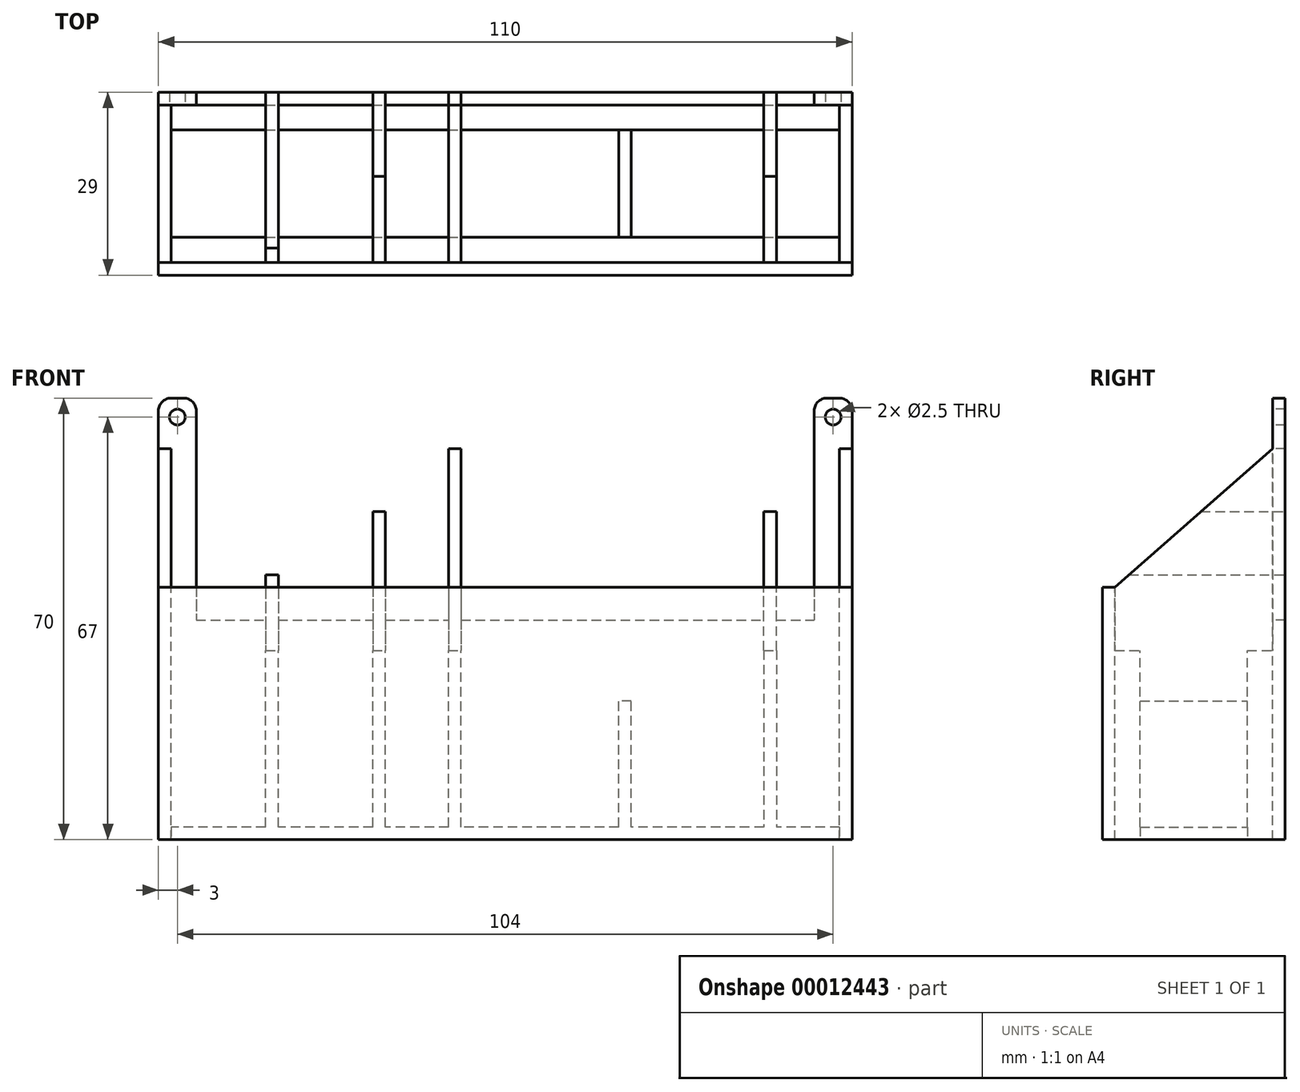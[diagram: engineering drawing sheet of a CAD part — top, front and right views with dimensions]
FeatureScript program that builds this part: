
annotation { "Feature Type Name" : "Feature", "Feature Type Description" : "" }
export const myFeature = defineFeature(function(context is Context, id is Id, definition is map)
    precondition{}
    {
        {
            var Q0;
            Q0=qCreatedBy(makeId("Front.planeOp"),FACE);
            var sketch = newSketch(context, id + "F0", { "sketchPlane" : qUnion([Q0])});
            skLineSegment(sketch, "E0.bottom", {"start": v(0, 0) * mm, "end": v(-110, 0) * mm});
            skLineSegment(sketch, "E0.top", {"start": v(-2, 70) * mm, "end": v(-108, 70) * mm});
            skLineSegment(sketch, "E0.left", {"start": v(0, 0) * mm, "end": v(0, 68) * mm});
            skLineSegment(sketch, "E0.right", {"start": v(-110, 0) * mm, "end": v(-110, 68) * mm});
            skPoint(sketch, "E1.visualSharp", {"position": v(0, 70) * mm});
            skArc(sketch, "E1.filletArc", {"start": v(0, 68) * mm, "mid": v(-0.59, 69.41) * mm, "end": v(-2, 70) * mm});
            skPoint(sketch, "E2.visualSharp", {"position": v(-110, 70) * mm});
            skArc(sketch, "E2.filletArc", {"start": v(-108, 70) * mm, "mid": v(-109.41, 69.41) * mm, "end": v(-110, 68) * mm});
            skSolve(sketch);
        }
        {
            var Q0;
            Q0 = qSketchRegion(id + "F0", true);
            extrude(context, id + "F1", {"entities" : qUnion([Q0]), "oppositeDirection" : true, "depth" : 2 * mm});
        }
        {
            var Q0;
            Q0=makeQuery(id+"F1.opExtrude","CAP_FACE",FACE,{"disambiguationData":[OSD([sQuery(id+"F0.wireOp",EDGE,"E0.bottom"),sQuery(id+"F0.wireOp",EDGE,"E0.top"),sQuery(id+"F0.wireOp",EDGE,"E0.left"),sQuery(id+"F0.wireOp",EDGE,"E0.right")])],"isStart":true});
            var sketch = newSketch(context, id + "F2", { "sketchPlane" : qUnion([Q0])});
            skLineSegment(sketch, "E3.bottom", {"start": v(-110, 2) * mm, "end": v(0, 2) * mm});
            skLineSegment(sketch, "E3.top", {"start": v(-110, 0) * mm, "end": v(0, 0) * mm});
            skLineSegment(sketch, "E3.left", {"start": v(-110, 2) * mm, "end": v(-110, 0) * mm});
            skLineSegment(sketch, "E3.right", {"start": v(0, 2) * mm, "end": v(0, 0) * mm});
            skLineSegment(sketch, "E4.bottom", {"start": v(0, 2) * mm, "end": v(-2, 2) * mm});
            skLineSegment(sketch, "E4.top", {"start": v(0, 62) * mm, "end": v(-2, 62) * mm});
            skLineSegment(sketch, "E4.left", {"start": v(0, 2) * mm, "end": v(0, 62) * mm});
            skLineSegment(sketch, "E4.right", {"start": v(-2, 2) * mm, "end": v(-2, 62) * mm});
            skLineSegment(sketch, "E5.bottom", {"start": v(-110, 2) * mm, "end": v(-108, 2) * mm});
            skLineSegment(sketch, "E5.top", {"start": v(-110, 62) * mm, "end": v(-108, 62) * mm});
            skLineSegment(sketch, "E5.left", {"start": v(-110, 2) * mm, "end": v(-110, 62) * mm});
            skLineSegment(sketch, "E5.right", {"start": v(-108, 2) * mm, "end": v(-108, 62) * mm});
            skLineSegment(sketch, "E6.bottom", {"start": v(-93, 42) * mm, "end": v(-91, 42) * mm});
            skLineSegment(sketch, "E6.top", {"start": v(-93, 2) * mm, "end": v(-91, 2) * mm});
            skLineSegment(sketch, "E6.left", {"start": v(-93, 42) * mm, "end": v(-93, 2) * mm});
            skLineSegment(sketch, "E6.right", {"start": v(-91, 42) * mm, "end": v(-91, 2) * mm});
            skLineSegment(sketch, "E7.bottom", {"start": v(-76, 52) * mm, "end": v(-74, 52) * mm});
            skLineSegment(sketch, "E7.top", {"start": v(-76, 2) * mm, "end": v(-74, 2) * mm});
            skLineSegment(sketch, "E7.left", {"start": v(-76, 52) * mm, "end": v(-76, 2) * mm});
            skLineSegment(sketch, "E7.right", {"start": v(-74, 52) * mm, "end": v(-74, 2) * mm});
            skLineSegment(sketch, "E8.bottom", {"start": v(-64, 62) * mm, "end": v(-62, 62) * mm});
            skLineSegment(sketch, "E8.top", {"start": v(-64, 2) * mm, "end": v(-62, 2) * mm});
            skLineSegment(sketch, "E8.left", {"start": v(-64, 62) * mm, "end": v(-64, 2) * mm});
            skLineSegment(sketch, "E8.right", {"start": v(-62, 62) * mm, "end": v(-62, 2) * mm});
            skLineSegment(sketch, "E9.bottom", {"start": v(-37, 22) * mm, "end": v(-35, 22) * mm});
            skLineSegment(sketch, "E9.top", {"start": v(-37, 2) * mm, "end": v(-35, 2) * mm});
            skLineSegment(sketch, "E9.left", {"start": v(-37, 22) * mm, "end": v(-37, 2) * mm});
            skLineSegment(sketch, "E9.right", {"start": v(-35, 22) * mm, "end": v(-35, 2) * mm});
            skLineSegment(sketch, "E10.bottom", {"start": v(-12, 2) * mm, "end": v(-14, 2) * mm});
            skLineSegment(sketch, "E10.top", {"start": v(-12, 52) * mm, "end": v(-14, 52) * mm});
            skLineSegment(sketch, "E10.left", {"start": v(-12, 2) * mm, "end": v(-12, 52) * mm});
            skLineSegment(sketch, "E10.right", {"start": v(-14, 2) * mm, "end": v(-14, 52) * mm});
            skSolve(sketch);
        }
        {
            var Q0;
            Q0 = qSketchRegion(id + "F2", true);
            extrude(context, id + "F3", {"entities" : qUnion([Q0]), "operationType" : NewBodyOperationType.ADD, "depth" : 25 * mm});
        }
        {
            var Q0;
            Q0=makeQuery(id+"F3.opExtrude","CAP_FACE",FACE,{"disambiguationData":[OSD([sQuery(id+"F2.wireOp",EDGE,"E3.bottom"),sQuery(id+"F2.wireOp",EDGE,"E3.top"),sQuery(id+"F2.wireOp",EDGE,"E3.left"),sQuery(id+"F2.wireOp",EDGE,"E3.right"),sQuery(id+"F2.wireOp",EDGE,"E4.top"),sQuery(id+"F2.wireOp",EDGE,"E4.left"),sQuery(id+"F2.wireOp",EDGE,"E4.right"),sQuery(id+"F2.wireOp",EDGE,"E5.top"),sQuery(id+"F2.wireOp",EDGE,"E5.left"),sQuery(id+"F2.wireOp",EDGE,"E5.right"),sQuery(id+"F2.wireOp",EDGE,"E6.bottom"),sQuery(id+"F2.wireOp",EDGE,"E6.left"),sQuery(id+"F2.wireOp",EDGE,"E6.right"),sQuery(id+"F2.wireOp",EDGE,"E7.bottom"),sQuery(id+"F2.wireOp",EDGE,"E7.left"),sQuery(id+"F2.wireOp",EDGE,"E7.right"),sQuery(id+"F2.wireOp",EDGE,"E8.bottom"),sQuery(id+"F2.wireOp",EDGE,"E8.left"),sQuery(id+"F2.wireOp",EDGE,"E8.right"),sQuery(id+"F2.wireOp",EDGE,"E9.bottom"),sQuery(id+"F2.wireOp",EDGE,"E9.left"),sQuery(id+"F2.wireOp",EDGE,"E9.right")])],"isStart":false});
            var sketch = newSketch(context, id + "F4", { "sketchPlane" : qUnion([Q0])});
            skLineSegment(sketch, "E11.bottom", {"start": v(-110, 0) * mm, "end": v(0, 0) * mm});
            skLineSegment(sketch, "E11.top", {"start": v(-110, 40) * mm, "end": v(0, 40) * mm});
            skLineSegment(sketch, "E11.left", {"start": v(-110, 0) * mm, "end": v(-110, 40) * mm});
            skLineSegment(sketch, "E11.right", {"start": v(0, 0) * mm, "end": v(0, 40) * mm});
            skSolve(sketch);
        }
        {
            var Q0;
            Q0 = qSketchRegion(id + "F4", true);
            extrude(context, id + "F5", {"entities" : qUnion([Q0]), "operationType" : NewBodyOperationType.ADD, "depth" : 2 * mm});
        }
        {
            var Q0;
            Q0=makeQuery(id+"F1.opExtrude","CAP_FACE",FACE,{"disambiguationData":[OSD([sQuery(id+"F0.wireOp",EDGE,"E0.bottom"),sQuery(id+"F0.wireOp",EDGE,"E0.top"),sQuery(id+"F0.wireOp",EDGE,"E0.left"),sQuery(id+"F0.wireOp",EDGE,"E0.right")])],"isStart":true});
            var sketch = newSketch(context, id + "F6", { "sketchPlane" : qUnion([Q0])});
            skCircle(sketch, "E12", {"center": v(-107, 67) * mm, "radius": 1.25 * mm});
            skCircle(sketch, "E13", {"center": v(-3, 67) * mm, "radius": 1.25 * mm});
            skSolve(sketch);
        }
        {
            var Q0;
            Q0 = qSketchRegion(id + "F6", true);
            extrude(context, id + "F7", {"entities" : qUnion([Q0]), "operationType" : NewBodyOperationType.REMOVE, "oppositeDirection" : true, "depth" : 2 * mm});
        }
        {
            var Q0;
            Q0=makeQuery(id+"F5.boolean.opBoolean","MERGE",FACE,{"derivedFrom":[makeQuery(id+"F3.boolean.opBoolean","MERGE",FACE,{"derivedFrom":[makeQuery(id+"F1.opExtrude","SWEPT_FACE",FACE,{"disambiguationData":[OSD([sQuery(id+"F0.wireOp",EDGE,"E0.right")])]}),makeQuery(id+"F3.opExtrude","SWEPT_FACE",FACE,{"disambiguationData":[OSD([sQuery(id+"F2.wireOp",EDGE,"E3.left"),sQuery(id+"F2.wireOp",EDGE,"E5.left")])]})]}),makeQuery(id+"F5.opExtrude","SWEPT_FACE",FACE,{"disambiguationData":[OSD([sQuery(id+"F4.wireOp",EDGE,"E11.left")])]})]});
            var sketch = newSketch(context, id + "F8", { "sketchPlane" : qUnion([Q0])});
            skLineSegment(sketch, "E14", {"start": v(25, 62) * mm, "end": v(25, 40) * mm});
            skLineSegment(sketch, "E15", {"start": v(25, 40) * mm, "end": v(0, 62) * mm});
            skLineSegment(sketch, "E16", {"start": v(0, 62) * mm, "end": v(25, 62) * mm});
            skSolve(sketch);
        }
        {
            var Q0;
            Q0 = qSketchRegion(id + "F8", true);
            extrude(context, id + "F9", {"entities" : qUnion([Q0]), "operationType" : NewBodyOperationType.REMOVE, "oppositeDirection" : true, "depth" : 110 * mm});
        }
        {
            var Q0;
            Q0=makeQuery(id+"F5.boolean.opBoolean","MERGE",FACE,{"derivedFrom":[makeQuery(id+"F3.boolean.opBoolean","MERGE",FACE,{"derivedFrom":[makeQuery(id+"F1.opExtrude","SWEPT_FACE",FACE,{"disambiguationData":[OSD([sQuery(id+"F0.wireOp",EDGE,"E0.bottom")])]}),makeQuery(id+"F3.opExtrude","SWEPT_FACE",FACE,{"disambiguationData":[OSD([sQuery(id+"F2.wireOp",EDGE,"E3.top")])]})]}),makeQuery(id+"F5.opExtrude","SWEPT_FACE",FACE,{"disambiguationData":[OSD([sQuery(id+"F4.wireOp",EDGE,"E11.bottom")])]})]});
            var sketch = newSketch(context, id + "F10", { "sketchPlane" : qUnion([Q0])});
            skLineSegment(sketch, "E17.bottom", {"start": v(-108, 0) * mm, "end": v(-2, 0) * mm});
            skLineSegment(sketch, "E17.top", {"start": v(-108, 4) * mm, "end": v(-2, 4) * mm});
            skLineSegment(sketch, "E17.left", {"start": v(-108, 0) * mm, "end": v(-108, 4) * mm});
            skLineSegment(sketch, "E17.right", {"start": v(-2, 0) * mm, "end": v(-2, 4) * mm});
            skLineSegment(sketch, "E18.bottom", {"start": v(-108, 21) * mm, "end": v(-2, 21) * mm});
            skLineSegment(sketch, "E18.top", {"start": v(-108, 25) * mm, "end": v(-2, 25) * mm});
            skLineSegment(sketch, "E18.left", {"start": v(-108, 21) * mm, "end": v(-108, 25) * mm});
            skLineSegment(sketch, "E18.right", {"start": v(-2, 21) * mm, "end": v(-2, 25) * mm});
            skSolve(sketch);
        }
        {
            var Q0;
            Q0 = qSketchRegion(id + "F10", true);
            extrude(context, id + "F11", {"entities" : qUnion([Q0]), "operationType" : NewBodyOperationType.REMOVE, "oppositeDirection" : true, "depth" : 30 * mm});
        }
        {
            var Q0;
            Q0=makeQuery(id+"F11.boolean.opBoolean","MERGE",FACE,{"derivedFrom":[makeQuery(id+"F1.opExtrude","CAP_FACE",FACE,{"disambiguationData":[OSD([sQuery(id+"F0.wireOp",EDGE,"E0.bottom"),sQuery(id+"F0.wireOp",EDGE,"E0.top"),sQuery(id+"F0.wireOp",EDGE,"E0.left"),sQuery(id+"F0.wireOp",EDGE,"E0.right"),sQuery(id+"F0.wireOp",EDGE,"E1.filletArc"),sQuery(id+"F0.wireOp",EDGE,"E2.filletArc")])],"isStart":true}),makeQuery(id+"F11.opExtrude","SWEPT_FACE",FACE,{"disambiguationData":[OSD([sQuery(id+"F10.wireOp",EDGE,"E17.bottom")])]})]});
            var sketch = newSketch(context, id + "F12", { "sketchPlane" : qUnion([Q0])});
            skLineSegment(sketch, "E19.bottom", {"start": v(-84, 70) * mm, "end": v(-6, 70) * mm});
            skLineSegment(sketch, "E19.top", {"start": v(-104, 34.81) * mm, "end": v(-6, 34.81) * mm});
            skLineSegment(sketch, "E19.left", {"start": v(-104, 68) * mm, "end": v(-104, 34.81) * mm});
            skLineSegment(sketch, "E19.right", {"start": v(-6, 68) * mm, "end": v(-6, 34.81) * mm});
            skLineSegment(sketch, "E20", {"start": v(-108, 70) * mm, "end": v(-106, 70) * mm});
            skLineSegment(sketch, "E21", {"start": v(-4, 70) * mm, "end": v(-2, 70) * mm});
            skArc(sketch, "E22.filletArc", {"start": v(-4, 70) * mm, "mid": v(-5.41, 69.41) * mm, "end": v(-6, 68) * mm});
            skArc(sketch, "E23.filletArc", {"start": v(-104, 68) * mm, "mid": v(-104.59, 69.41) * mm, "end": v(-106, 70) * mm});
            skSolve(sketch);
        }
        {
            var Q0;
            {var subQ14=sQuery(id+"F12.wireOp",EDGE,"E19.bottom");Q0=makeQuery(id+"F12.imprint","IMPRINT",FACE,{"disambiguationData":[TD([[makeQuery(id+"F12.imprint","IMPRINT",EDGE,{"derivedFrom":subQ14}),1.0]])]});}
            extrude(context, id + "F13", {"entities" : qUnion([Q0]), "operationType" : NewBodyOperationType.REMOVE, "oppositeDirection" : true, "depth" : 2 * mm});
        }
    });
